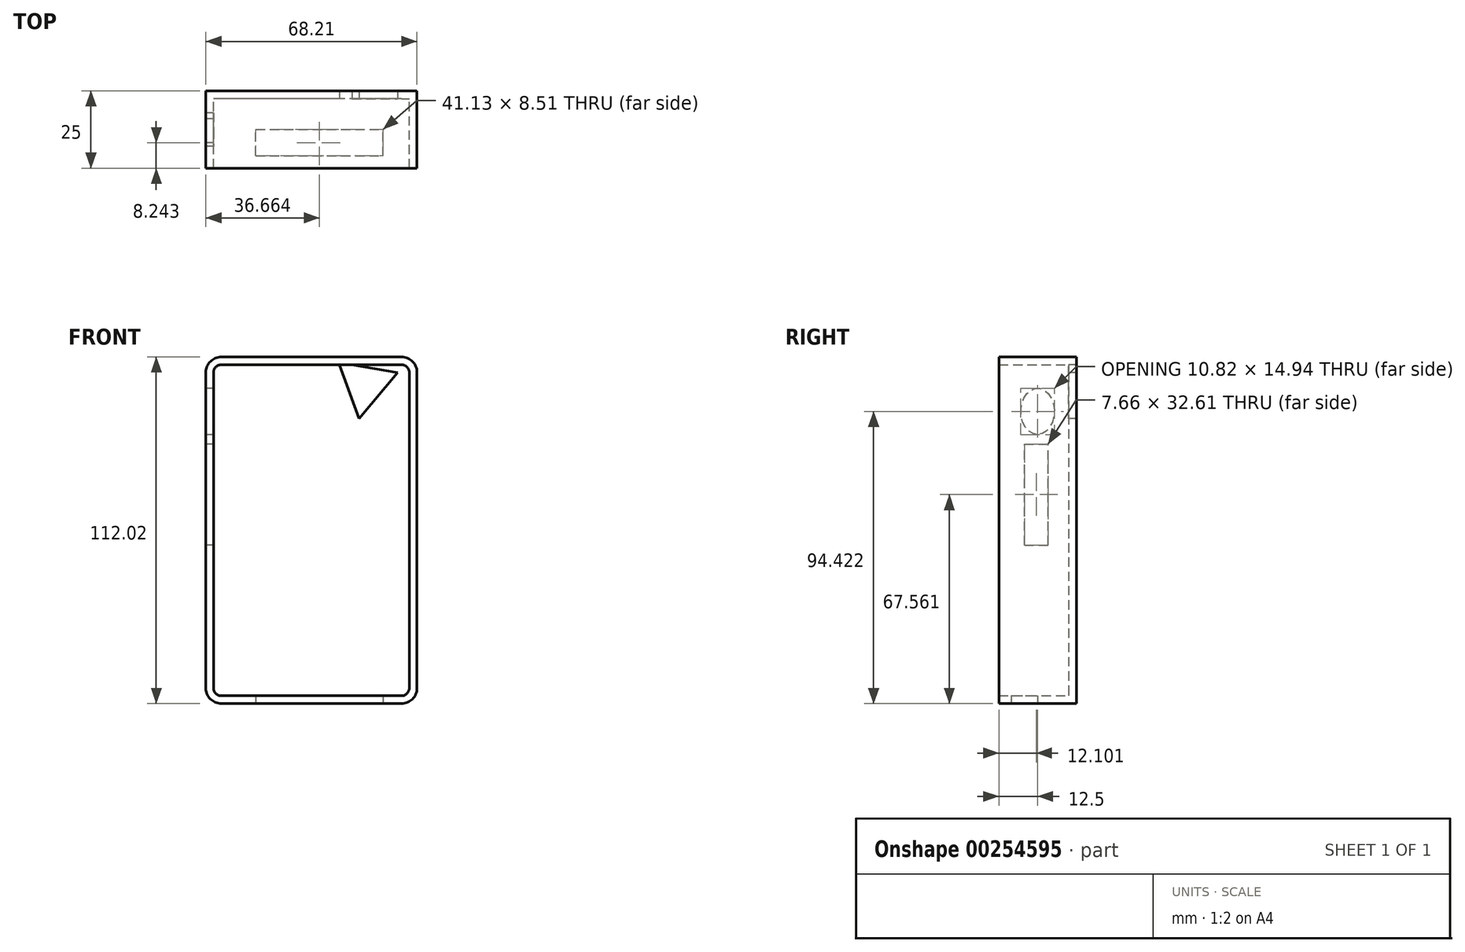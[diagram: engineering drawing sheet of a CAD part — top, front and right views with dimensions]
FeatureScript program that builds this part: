
annotation { "Feature Type Name" : "Feature", "Feature Type Description" : "" }
export const myFeature = defineFeature(function(context is Context, id is Id, definition is map)
    precondition{}
    {
        {
            var Q0;
            Q0=qCreatedBy(makeId("Front.planeOp"),FACE);
            var sketch = newSketch(context, id + "F0", { "sketchPlane" : qUnion([Q0])});
            skLineSegment(sketch, "E0.bottom", {"start": v(30.78, 56.01) * mm, "end": v(-37.43, 56.01) * mm});
            skLineSegment(sketch, "E0.top", {"start": v(30.78, -56.01) * mm, "end": v(-37.43, -56.01) * mm});
            skLineSegment(sketch, "E0.left", {"start": v(30.78, 56.01) * mm, "end": v(30.78, -56.01) * mm});
            skLineSegment(sketch, "E0.right", {"start": v(-37.43, 56.01) * mm, "end": v(-37.43, -56.01) * mm});
            skPoint(sketch, "E0.middle", {"position": v(-3.33, 0) * mm});
            skSolve(sketch);
        }
        {
            var Q0;
            Q0 = qSketchRegion(id + "F0", true);
            extrude(context, id + "F1", {"entities" : qUnion([Q0]), "depth" : 25 * mm, "symmetric" : true});
        }
        {
            var Q0;
            Q0=makeQuery(id+"F1.opExtrude","SWEPT_EDGE",EDGE,{"disambiguationData":[OSD([sQuery(id+"F0.wireOp",EDGE,"E0.bottom"),sQuery(id+"F0.wireOp",EDGE,"E0.right")])]});
            var Q1;
            Q1=makeQuery(id+"F1.opExtrude","SWEPT_EDGE",EDGE,{"disambiguationData":[OSD([sQuery(id+"F0.wireOp",EDGE,"E0.bottom"),sQuery(id+"F0.wireOp",EDGE,"E0.left")])]});
            var Q2;
            Q2=makeQuery(id+"F1.opExtrude","SWEPT_EDGE",EDGE,{"disambiguationData":[OSD([sQuery(id+"F0.wireOp",EDGE,"E0.top"),sQuery(id+"F0.wireOp",EDGE,"E0.left")])]});
            var Q3;
            Q3=makeQuery(id+"F1.opExtrude","SWEPT_EDGE",EDGE,{"disambiguationData":[OSD([sQuery(id+"F0.wireOp",EDGE,"E0.top"),sQuery(id+"F0.wireOp",EDGE,"E0.right")])]});
            fillet(context, id + "F2", {"entities" : qUnion([Q0, Q1, Q2, Q3]), "radius" : 5 * mm, "tangentPropagation" : true, "allowEdgeOverflow" : false});
        }
        {
            var Q0;
            Q0=makeQuery(id+"F1.opExtrude","CAP_FACE",FACE,{"disambiguationData":[OSD([sQuery(id+"F0.wireOp",EDGE,"E0.bottom"),sQuery(id+"F0.wireOp",EDGE,"E0.top"),sQuery(id+"F0.wireOp",EDGE,"E0.left"),sQuery(id+"F0.wireOp",EDGE,"E0.right")])],"isStart":false});
            shell(context, id + "F3", {"entities" : qUnion([Q0]), "thickness" : 2.5 * mm});
        }
        {
            var Q0;
            Q0=makeQuery(id+"F3.opShell","OFFSET_FACE",FACE,{"disambiguationData":[OSD([sQuery(id+"F0.wireOp",EDGE,"E0.bottom"),sQuery(id+"F0.wireOp",EDGE,"E0.top"),sQuery(id+"F0.wireOp",EDGE,"E0.left"),sQuery(id+"F0.wireOp",EDGE,"E0.right")])]});
            var sketch = newSketch(context, id + "F4", { "sketchPlane" : qUnion([Q0])});
            skCircle(sketch, "E1.cCircle", {"center": v(14.04, 47.1) * mm, "radius": 5.57 * mm, "construction": true});
            skLineSegment(sketch, "E1.0", {"start": v(12.1, 36.14) * mm, "end": v(5.5, 54.27) * mm});
            skLineSegment(sketch, "E1.1", {"start": v(5.5, 54.27) * mm, "end": v(24.5, 50.91) * mm});
            skLineSegment(sketch, "E1.2", {"start": v(24.5, 50.91) * mm, "end": v(12.1, 36.14) * mm});
            skPoint(sketch, "E1.0.midPoint", {"position": v(8.8, 45.2) * mm});
            skSolve(sketch);
        }
        {
            var Q0;
            {var subQ0=sQuery(id+"F4.wireOp",EDGE,"E1.2");Q0=makeQuery(id+"F4.imprint","IMPRINT",FACE,{"disambiguationData":[TD([[makeQuery(id+"F4.imprint","IMPRINT",EDGE,{"derivedFrom":subQ0}),-1.0]])]});}
            extrude(context, id + "F5", {"entities" : qUnion([Q0]), "operationType" : NewBodyOperationType.REMOVE, "oppositeDirection" : true, "depth" : 25 * mm, "symmetric" : true});
        }
        {
            var Q0;
            Q0=makeQuery(id+"F1.opExtrude","SWEPT_FACE",FACE,{"disambiguationData":[OSD([sQuery(id+"F0.wireOp",EDGE,"E0.right")])]});
            var sketch = newSketch(context, id + "F6", { "sketchPlane" : qUnion([Q0])});
            skEllipse(sketch, "E2", {"center": v(0, 38.41) * mm, "majorRadius": 7.47 * mm, "minorRadius": 5.41 * mm, "majorAxis": v(0, -1)});
            skSolve(sketch);
        }
        {
            var Q0;
            Q0=makeQuery(id+"F6.imprint","IMPRINT",FACE,{"disambiguationData":[TD([[makeQuery(id+"F6.imprint","IMPRINT",EDGE,{"derivedFrom":sQuery(id+"F6.wireOp",EDGE,"E2")}),1.0]])]});
            extrude(context, id + "F7", {"entities" : qUnion([Q0]), "operationType" : NewBodyOperationType.REMOVE, "oppositeDirection" : true, "depth" : 25 * mm, "symmetric" : true});
        }
        {
            var Q0;
            Q0=makeQuery(id+"F1.opExtrude","SWEPT_FACE",FACE,{"disambiguationData":[OSD([sQuery(id+"F0.wireOp",EDGE,"E0.top")])]});
            var sketch = newSketch(context, id + "F8", { "sketchPlane" : qUnion([Q0])});
            skLineSegment(sketch, "E3.bottom", {"start": v(-21.33, 8.51) * mm, "end": v(19.8, 8.51) * mm});
            skLineSegment(sketch, "E3.top", {"start": v(-21.33, 0) * mm, "end": v(19.8, 0) * mm});
            skLineSegment(sketch, "E3.left", {"start": v(-21.33, 8.51) * mm, "end": v(-21.33, 0) * mm});
            skLineSegment(sketch, "E3.right", {"start": v(19.8, 8.51) * mm, "end": v(19.8, 0) * mm});
            skSolve(sketch);
        }
        {
            var Q0;
            Q0=makeQuery(id+"F8.imprint","IMPRINT",FACE,{"disambiguationData":[TD([[makeQuery(id+"F8.imprint","IMPRINT",EDGE,{"derivedFrom":sQuery(id+"F8.wireOp",EDGE,"E3.bottom")}),-1.0]])]});
            extrude(context, id + "F9", {"entities" : qUnion([Q0]), "operationType" : NewBodyOperationType.REMOVE, "oppositeDirection" : true, "depth" : 25 * mm, "symmetric" : true});
        }
        {
            var Q0;
            Q0=makeQuery(id+"F1.opExtrude","SWEPT_FACE",FACE,{"disambiguationData":[OSD([sQuery(id+"F0.wireOp",EDGE,"E0.right")])]});
            var sketch = newSketch(context, id + "F10", { "sketchPlane" : qUnion([Q0])});
            skLineSegment(sketch, "E4.bottom", {"start": v(-3.43, 27.85) * mm, "end": v(4.23, 27.85) * mm});
            skLineSegment(sketch, "E4.top", {"start": v(-3.43, -4.75) * mm, "end": v(4.23, -4.75) * mm});
            skLineSegment(sketch, "E4.left", {"start": v(-3.43, 27.85) * mm, "end": v(-3.43, -4.75) * mm});
            skLineSegment(sketch, "E4.right", {"start": v(4.23, 27.85) * mm, "end": v(4.23, -4.75) * mm});
            skSolve(sketch);
        }
        {
            var Q0;
            Q0=makeQuery(id+"F10.imprint","IMPRINT",FACE,{"disambiguationData":[TD([[makeQuery(id+"F10.imprint","IMPRINT",EDGE,{"derivedFrom":sQuery(id+"F10.wireOp",EDGE,"E4.bottom")}),-1.0]])]});
            extrude(context, id + "F11", {"entities" : qUnion([Q0]), "operationType" : NewBodyOperationType.REMOVE, "oppositeDirection" : true, "depth" : 25 * mm, "symmetric" : true});
        }
    });
